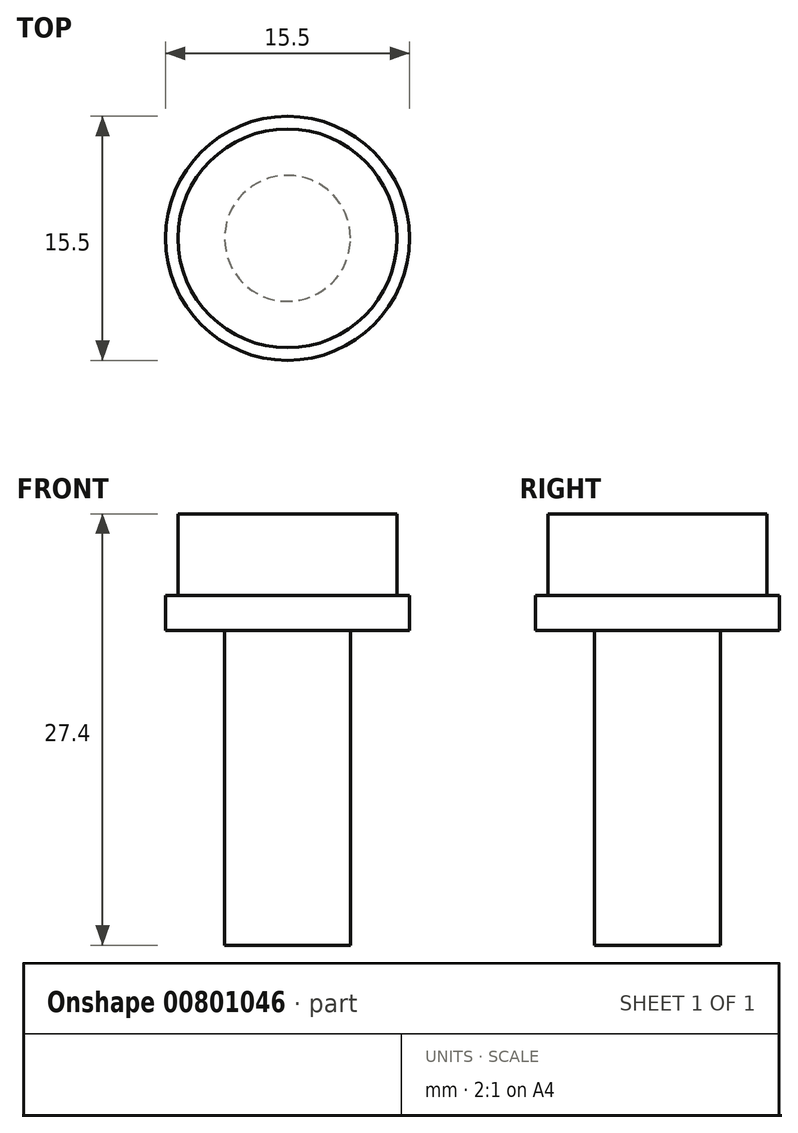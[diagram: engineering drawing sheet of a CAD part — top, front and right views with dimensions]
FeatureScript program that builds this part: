
annotation { "Feature Type Name" : "Feature", "Feature Type Description" : "" }
export const myFeature = defineFeature(function(context is Context, id is Id, definition is map)
    precondition{}
    {
        {
            var Q0;
            Q0=qCreatedBy(makeId("Front.planeOp"),FACE);
            var sketch = newSketch(context, id + "F0", { "sketchPlane" : qUnion([Q0])});
            skLineSegment(sketch, "E0", {"start": v(0, 0) * mm, "end": v(0, -27.4) * mm});
            skLineSegment(sketch, "E1", {"start": v(0, -27.4) * mm, "end": v(4, -27.4) * mm});
            skLineSegment(sketch, "E2", {"start": v(4, -27.4) * mm, "end": v(4, -7.4) * mm});
            skLineSegment(sketch, "E3", {"start": v(4, -7.4) * mm, "end": v(7.75, -7.4) * mm});
            skLineSegment(sketch, "E4", {"start": v(7.75, -7.4) * mm, "end": v(7.75, -5.2) * mm});
            skLineSegment(sketch, "E5", {"start": v(7.75, -5.2) * mm, "end": v(6.95, -5.2) * mm});
            skLineSegment(sketch, "E6", {"start": v(6.95, -5.2) * mm, "end": v(6.95, 0) * mm});
            skLineSegment(sketch, "E7", {"start": v(6.95, 0) * mm, "end": v(0, 0) * mm});
            skSolve(sketch);
        }
        {
            var Q0;
            Q0=makeQuery(id+"F0.imprint","IMPRINT",FACE,{"disambiguationData":[TD([[makeQuery(id+"F0.imprint","IMPRINT",EDGE,{"derivedFrom":sQuery(id+"F0.wireOp",EDGE,"E0")}),1.0]])]});
            var Q1;
            Q1=sQuery(id+"F0.wireOp",EDGE,"E0");
            revolve(context, id + "F1", {"surfaceOperationType" : NewSurfaceOperationType.NEW, "entities" : qUnion([Q0]), "axis" : qUnion([Q1]), "revolveType" : RevolveType.FULL});
        }
    });
